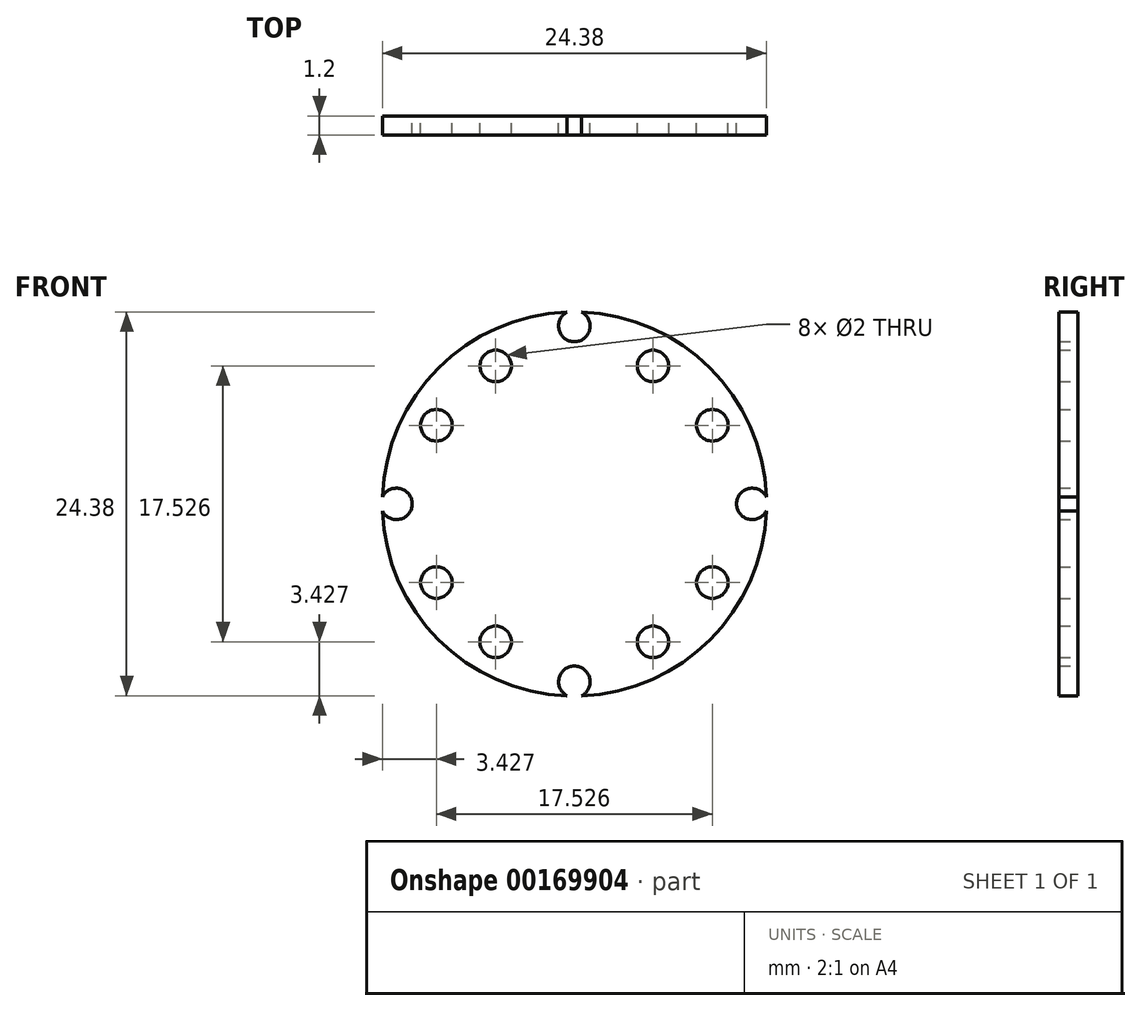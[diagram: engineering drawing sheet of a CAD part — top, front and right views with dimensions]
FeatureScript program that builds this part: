
annotation { "Feature Type Name" : "Feature", "Feature Type Description" : "" }
export const myFeature = defineFeature(function(context is Context, id is Id, definition is map)
    precondition{}
    {
        {
            var Q0;
            Q0=qCreatedBy(makeId("Front.planeOp"),FACE);
            var sketch = newSketch(context, id + "F0", { "sketchPlane" : qUnion([Q0])});
            skCircle(sketch, "E0", {"center": v(0, 0) * mm, "radius": 12.2 * mm});
            skCircle(sketch, "E1", {"center": v(0, 11.3) * mm, "radius": 1 * mm});
            skCircle(sketch, "E2.1.0", {"center": v(-11.3, 0) * mm, "radius": 1 * mm});
            skCircle(sketch, "E2.2.0", {"center": v(0, -11.3) * mm, "radius": 1 * mm});
            skCircle(sketch, "E3.1.3.0", {"center": v(11.3, 0) * mm, "radius": 1 * mm});
            skCircle(sketch, "E4", {"center": v(8.76, 5) * mm, "radius": 1 * mm});
            skCircle(sketch, "E5", {"center": v(5, 8.76) * mm, "radius": 1 * mm});
            skCircle(sketch, "E6.1.0", {"center": v(-8.76, 5) * mm, "radius": 1 * mm});
            skCircle(sketch, "E6.1.1", {"center": v(-5, 8.76) * mm, "radius": 1 * mm});
            skCircle(sketch, "E6.2.0", {"center": v(-5, -8.76) * mm, "radius": 1 * mm});
            skCircle(sketch, "E6.2.1", {"center": v(-8.76, -5) * mm, "radius": 1 * mm});
            skCircle(sketch, "E7.2.3.0", {"center": v(5, -8.76) * mm, "radius": 1 * mm});
            skCircle(sketch, "E7.3.3.0", {"center": v(8.76, -5) * mm, "radius": 1 * mm});
            skSolve(sketch);
        }
        {
            var Q0;
            {var subQ6=sQuery(id+"F0.wireOp",EDGE,"E2.1.0");Q0=makeQuery(id+"F0.imprint","IMPRINT",FACE,{"disambiguationData":[TD([[makeQuery(id+"F0.imprint","IMPRINT",EDGE,{"derivedFrom":subQ6}),-1.0]])]});}
            extrude(context, id + "F1", {"entities" : qUnion([Q0]), "depth" : 1.2 * mm});
        }
    });
